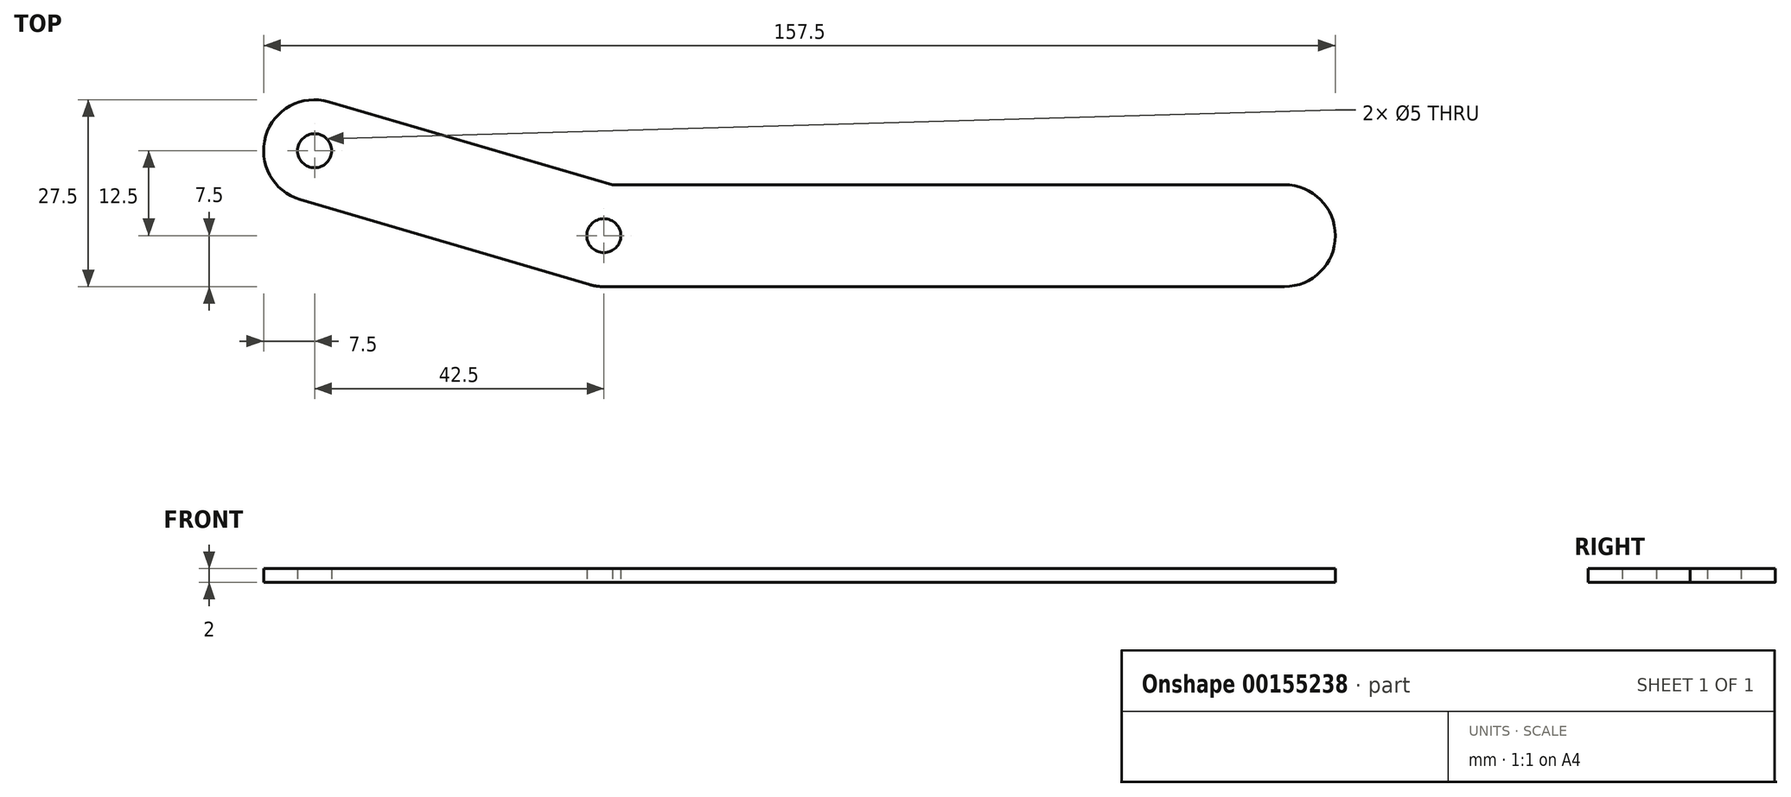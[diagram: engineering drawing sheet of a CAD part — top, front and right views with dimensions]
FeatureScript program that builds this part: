
annotation { "Feature Type Name" : "Feature", "Feature Type Description" : "" }
export const myFeature = defineFeature(function(context is Context, id is Id, definition is map)
    precondition{}
    {
        {
            var Q0;
            Q0=qCreatedBy(makeId("Top.planeOp"),FACE);
            var sketch = newSketch(context, id + "F0", { "sketchPlane" : qUnion([Q0])});
            skLineSegment(sketch, "E0.top", {"start": v(0, -15) * mm, "end": v(100, -15) * mm});
            skPoint(sketch, "E1.orphan", {"position": v(0, 0) * mm});
            skPoint(sketch, "E2.orphan", {"position": v(2.44, -1.4) * mm});
            skArc(sketch, "E3", {"start": v(100, -15) * mm, "mid": v(107.5, -7.5) * mm, "end": v(100, 0) * mm});
            skCircle(sketch, "E4", {"center": v(0, -7.5) * mm, "radius": 2.5 * mm});
            skArc(sketch, "E5", {"start": v(-40.38, 12.2) * mm, "mid": v(-49.7, 7.12) * mm, "end": v(-44.62, -2.2) * mm});
            skArc(sketch, "E6", {"start": v(-2.12, -14.7) * mm, "mid": v(-1.07, -14.92) * mm, "end": v(0, -15) * mm});
            skLineSegment(sketch, "E7", {"start": v(-40.38, 12.2) * mm, "end": v(1.25, -0.05) * mm});
            skLineSegment(sketch, "E8", {"start": v(-44.62, -2.2) * mm, "end": v(-2.12, -14.7) * mm});
            skLineSegment(sketch, "E9", {"start": v(100, 0) * mm, "end": v(1.25, -0.05) * mm});
            skCircle(sketch, "E10", {"center": v(-42.5, 5) * mm, "radius": 2.5 * mm});
            skSolve(sketch);
        }
        {
            var Q0;
            Q0 = qSketchRegion(id + "F0", true);
            extrude(context, id + "F1", {"entities" : qUnion([Q0]), "depth" : 2 * mm});
        }
    });
